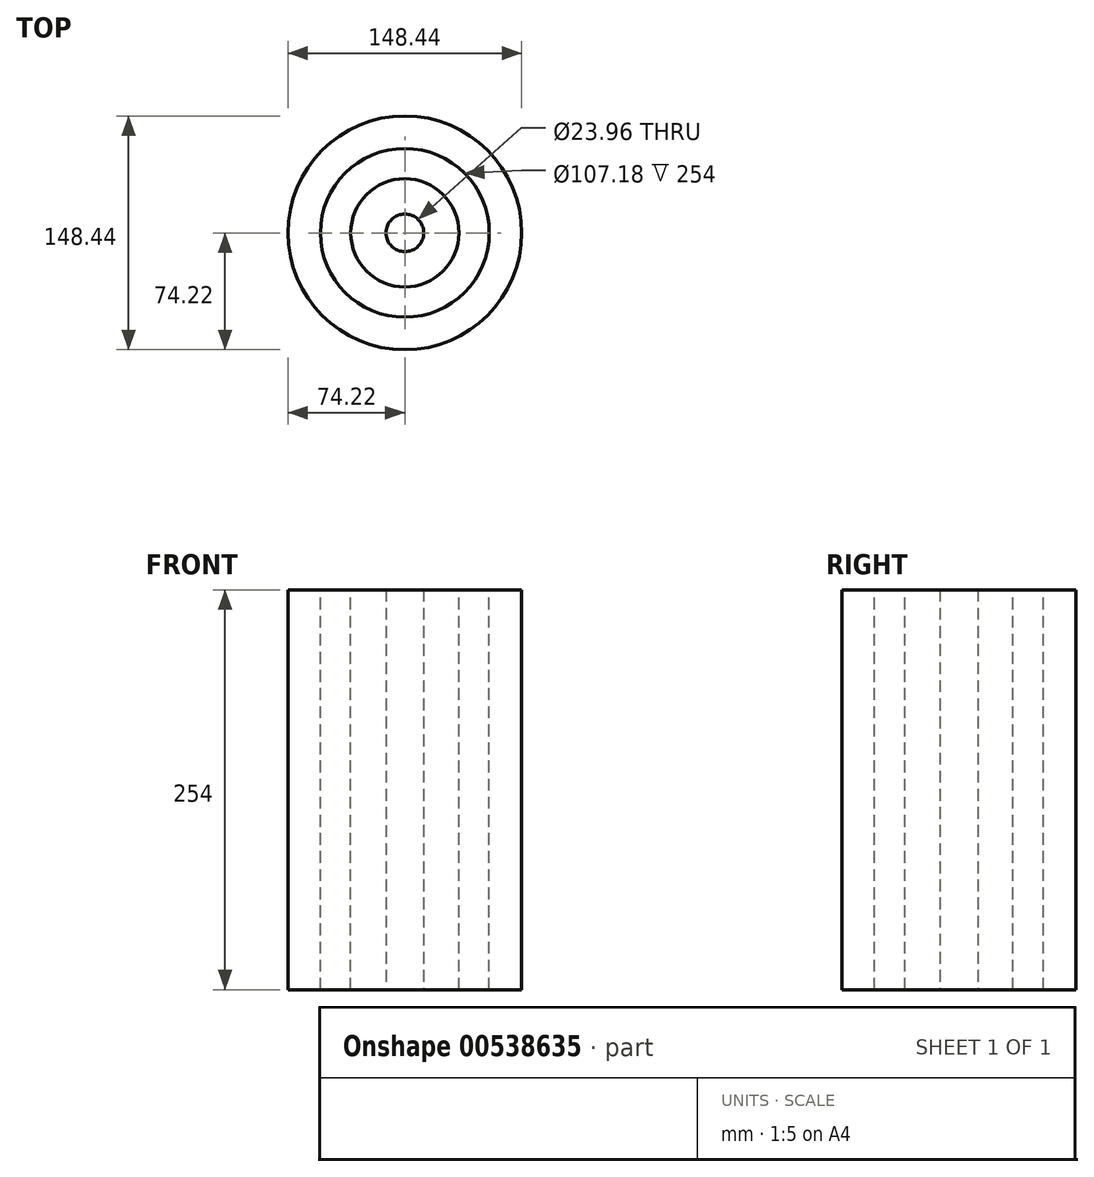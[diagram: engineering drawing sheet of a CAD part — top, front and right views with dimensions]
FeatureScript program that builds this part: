
annotation { "Feature Type Name" : "Feature", "Feature Type Description" : "" }
export const myFeature = defineFeature(function(context is Context, id is Id, definition is map)
    precondition{}
    {
        {
            var Q0;
            Q0=qCreatedBy(makeId("Top.planeOp"),FACE);
            var sketch = newSketch(context, id + "F0", { "sketchPlane" : qUnion([Q0])});
            skCircle(sketch, "E0", {"center": v(0, 0) * mm, "radius": 74.22 * mm});
            skSolve(sketch);
        }
        {
            var Q0;
            Q0=makeQuery(id+"F0.imprint","IMPRINT",FACE,{"disambiguationData":[TD([[makeQuery(id+"F0.imprint","IMPRINT",EDGE,{"derivedFrom":sQuery(id+"F0.wireOp",EDGE,"E0")}),1.0]])]});
            extrude(context, id + "F1", {"entities" : qUnion([Q0]), "depth" : 254 * mm, "offsetDistance" : 25.4 * mm});
        }
        {
            var Q0;
            Q0=makeQuery(id+"F1.opExtrude","CAP_FACE",FACE,{"disambiguationData":[OSD([sQuery(id+"F0.wireOp",EDGE,"E0")])],"isStart":true});
            var sketch = newSketch(context, id + "F2", { "sketchPlane" : qUnion([Q0])});
            skCircle(sketch, "E1", {"center": v(0, 0) * mm, "radius": 11.98 * mm});
            skSolve(sketch);
        }
        {
            var Q0;
            Q0=makeQuery(id+"F2.imprint","IMPRINT",FACE,{"disambiguationData":[TD([[makeQuery(id+"F2.imprint","IMPRINT",EDGE,{"derivedFrom":sQuery(id+"F2.wireOp",EDGE,"E1")}),1.0]])]});
            extrude(context, id + "F3", {"entities" : qUnion([Q0]), "operationType" : NewBodyOperationType.REMOVE, "oppositeDirection" : true, "depth" : 25.4 * mm, "offsetDistance" : 25.4 * mm});
        }
        {
            var Q0;
            Q0=makeQuery(id+"F3.boolean.opBoolean","COPY",FACE,{"derivedFrom":makeQuery(id+"F3.opExtrude","CAP_FACE",FACE,{"disambiguationData":[OSD([sQuery(id+"F2.wireOp",EDGE,"E1")])],"isStart":false})});
            extrude(context, id + "F4", {"entities" : qUnion([Q0]), "operationType" : NewBodyOperationType.REMOVE, "oppositeDirection" : true, "depth" : 228.6 * mm, "offsetDistance" : 25.4 * mm});
        }
        {
            var Q0;
            Q0=makeQuery(id+"F1.opExtrude","CAP_FACE",FACE,{"disambiguationData":[OSD([sQuery(id+"F0.wireOp",EDGE,"E0")])],"isStart":false});
            var sketch = newSketch(context, id + "F5", { "sketchPlane" : qUnion([Q0])});
            skCircle(sketch, "E2", {"center": v(0, 0) * mm, "radius": 34.37 * mm});
            skCircle(sketch, "E3", {"center": v(0, 0) * mm, "radius": 53.6 * mm});
            skSolve(sketch);
        }
        {
            var Q0;
            Q0=makeQuery(id+"F5.imprint","IMPRINT",FACE,{"disambiguationData":[TD([[makeQuery(id+"F5.imprint","IMPRINT",EDGE,{"derivedFrom":sQuery(id+"F5.wireOp",EDGE,"E2")}),-1.0]])]});
            extrude(context, id + "F6", {"entities" : qUnion([Q0]), "operationType" : NewBodyOperationType.REMOVE, "oppositeDirection" : true, "depth" : 254 * mm, "offsetDistance" : 25.4 * mm});
        }
    });
